# Revit family: SWC_Chartham 450 basin 2TH CHWB103 Rev00
name_source: partatom
category: Generic Models
revit_build: Autodesk Revit 2015 (Build: 20140606_1530(x64)
units: mm (PartAtom-declared; Revit-internal decimal feet)

## types (1)
- SWC_WHB_CHWB103
    Basin mounting = Wall Mounted
    Brand = SanCeram
    Help = http://www.theswc.co.uk
    Manufacturer URL = www.theswc.co.uk
    NBS Reference Code = N13 - 335
    NBS Reference Description = WASH BASINS
    Name = Chartham 450 wall hung basin, 2TH
    Nominal Depth = 195 mm
    Nominal Length = 360 mm
    Nominal Width = 450 mm
    Overflow = Central overflow
    Pedestal = Full pedestal - CHWB110 / Semi-pedestal - CHWB111 (Supplied seperatly)
    Primary Finishes = Alpine White
    Primary Material = Vitreous China
    Product Family = Sanitary
    Product Group = Wall Hung Basin
    Product Information = http://www.theswc.co.uk
    Product SKU = CHWB103
    Spare Parts = http://www.theswc.co.uk
    Tap Holes = Two tap holes
    Wash hand basin type = Hand wash
    Waste size = 1 1/4"
    Waste type = Slotted
    Weight = 10 kg

## geometry (parser evidence)
native form markers: Blend x4, Sweep x16
no freeform markers — native parametric forms only
